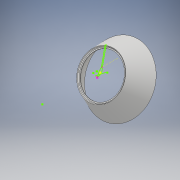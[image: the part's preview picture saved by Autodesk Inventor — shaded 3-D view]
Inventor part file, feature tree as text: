
AUTODESK INVENTOR PART (.ipt)
format: ipt  version: 2018 (Build 220112000, 112)  size: 195,072 bytes
history: native  units: mm
features: sketch x3, revolve x1
ambient origin geometry x8: Origin, YZ Plane, XZ Plane, XY Plane, X Axis, Y Axis, Z Axis, Center Point
bodies: Body1 (feature_tree)
feature tree (4):
  sketch  "Sketch68"  dims[d600=1.4mm d601=1.4mm]
  sketch  "Sketch184"  dims[d603=1.265mm]
  revolve  "Revolution5"  [1 undecoded]
  sketch  "Sketch213"  dims[d604=90.0deg d21=1.0mm d22=1.0mm]
note: 1 required parameter value undecoded (feature->parameter linkage not recoverable at this tier; creation-order binding heuristic only, values carry confidence <= 0.55)
